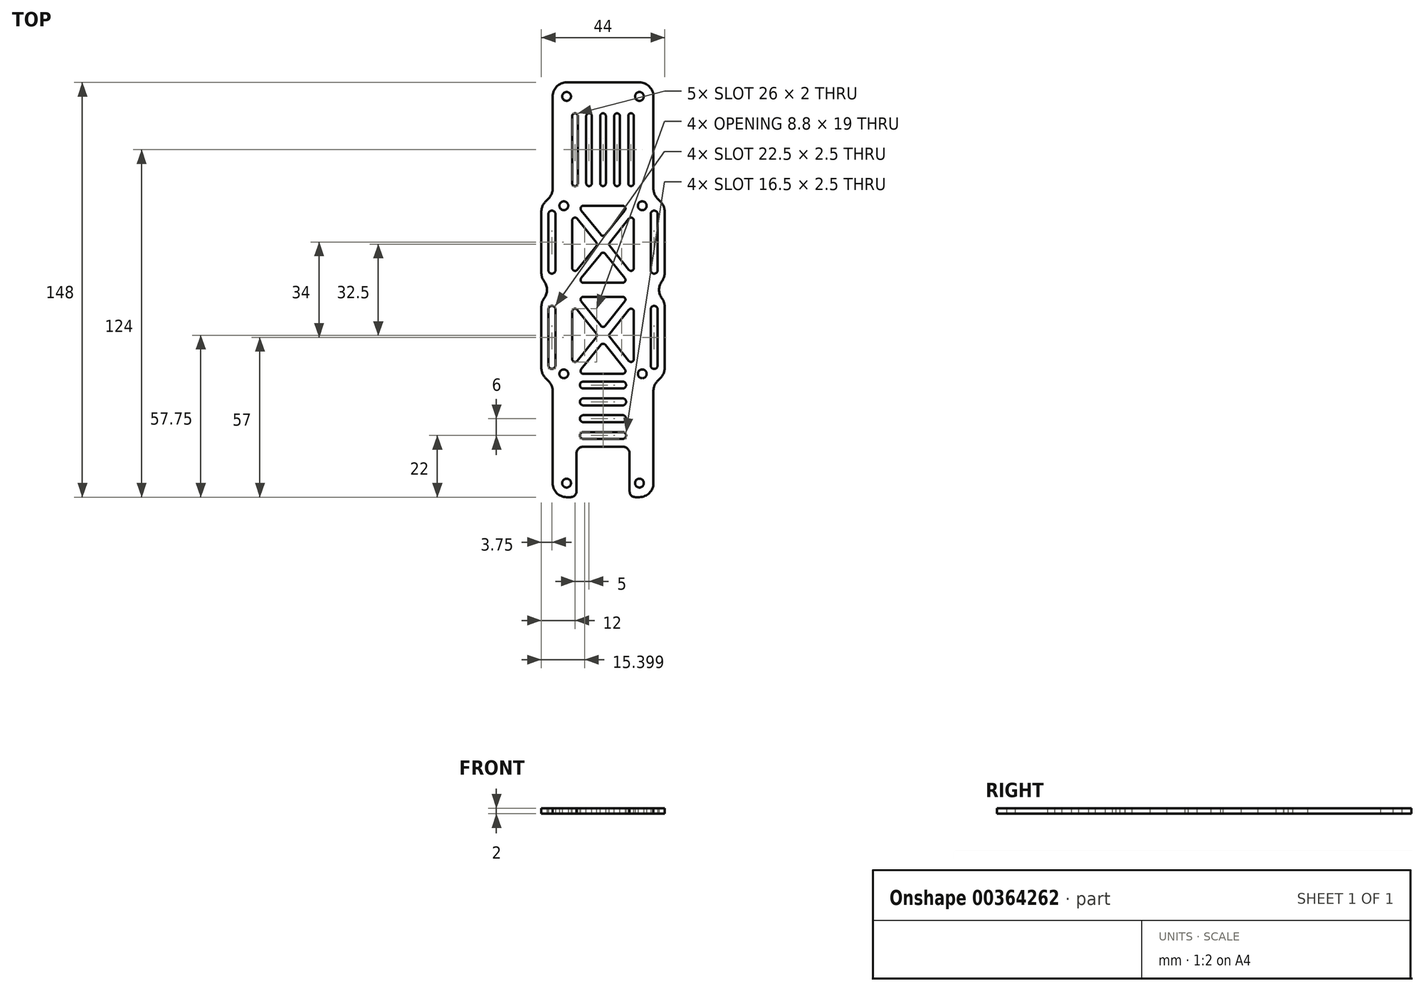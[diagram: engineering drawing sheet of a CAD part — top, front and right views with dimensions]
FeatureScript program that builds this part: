
annotation { "Feature Type Name" : "Feature", "Feature Type Description" : "" }
export const myFeature = defineFeature(function(context is Context, id is Id, definition is map)
    precondition{}
    {
        {
            var Q0;
            Q0=qCreatedBy(makeId("Top.planeOp"),FACE);
            var sketch = newSketch(context, id + "F0", { "sketchPlane" : qUnion([Q0])});
            skLineSegment(sketch, "E0", {"start": v(0, 74) * mm, "end": v(-13, 74) * mm});
            skLineSegment(sketch, "E1", {"start": v(-18, 69) * mm, "end": v(-18, 36.07) * mm});
            skLineSegment(sketch, "E2", {"start": v(-84.26, 70.7) * mm, "end": v(0, 0) * mm, "construction": true});
            skCircle(sketch, "E3", {"center": v(0, 0) * mm, "radius": 110 * mm, "construction": true});
            skPoint(sketch, "E4.visualSharp", {"position": v(-18, 74) * mm});
            skArc(sketch, "E4.filletArc", {"start": v(-13, 74) * mm, "mid": v(-16.54, 72.54) * mm, "end": v(-18, 69) * mm});
            skCircle(sketch, "E5", {"center": v(-13, 69) * mm, "radius": 1.57 * mm});
            skCircle(sketch, "E6.MirrorC", {"center": v(13, 69) * mm, "radius": 1.57 * mm});
            skArc(sketch, "E7.MirrorCS", {"start": v(13, 74) * mm, "mid": v(16.54, 72.54) * mm, "end": v(18, 69) * mm});
            skLineSegment(sketch, "E8.MirrorCS", {"start": v(0, 74) * mm, "end": v(13, 74) * mm});
            skLineSegment(sketch, "E9.MirrorCS", {"start": v(18, 69) * mm, "end": v(18, 36.07) * mm});
            skPoint(sketch, "E10.MirrorP", {"position": v(18, 74) * mm});
            skLineSegment(sketch, "E11.MirrorCS", {"start": v(84.26, 70.7) * mm, "end": v(0, 0) * mm, "construction": true});
            skArc(sketch, "E12.MirrorCS", {"start": v(-13, -74) * mm, "mid": v(-16.54, -72.54) * mm, "end": v(-18, -69) * mm});
            skLineSegment(sketch, "E13.MirrorCS", {"start": v(-11.5, -74) * mm, "end": v(-13, -74) * mm});
            skArc(sketch, "E14.MirrorCS", {"start": v(13, -74) * mm, "mid": v(16.54, -72.54) * mm, "end": v(18, -69) * mm});
            skLineSegment(sketch, "E15.MirrorCS", {"start": v(11.5, -74) * mm, "end": v(13, -74) * mm});
            skPoint(sketch, "E16.MirrorP", {"position": v(18, -74) * mm});
            skPoint(sketch, "E17.MirrorP", {"position": v(-18, -74) * mm});
            skLineSegment(sketch, "E18.MirrorCS", {"start": v(-18, -69) * mm, "end": v(-18, -36.07) * mm});
            skLineSegment(sketch, "E19.MirrorCS", {"start": v(18, -69) * mm, "end": v(18, -36.07) * mm});
            skCircle(sketch, "E20", {"center": v(-84.26, 70.7) * mm, "radius": 64.5 * mm, "construction": true});
            skCircle(sketch, "E21", {"center": v(-14, 30) * mm, "radius": 1.57 * mm});
            skCircle(sketch, "E22.MirrorC", {"center": v(14, 30) * mm, "radius": 1.57 * mm});
            skCircle(sketch, "E23.MirrorC", {"center": v(14, -30) * mm, "radius": 1.57 * mm});
            skCircle(sketch, "E24.MirrorC", {"center": v(-14, -30) * mm, "radius": 1.57 * mm});
            skLineSegment(sketch, "E25", {"start": v(-9.5, -72) * mm, "end": v(-9.5, -58.5) * mm});
            skLineSegment(sketch, "E26", {"start": v(-7, -56) * mm, "end": v(0, -56) * mm});
            skPoint(sketch, "E27.visualSharp", {"position": v(-9.5, -56) * mm});
            skArc(sketch, "E27.filletArc", {"start": v(-7, -56) * mm, "mid": v(-8.77, -56.73) * mm, "end": v(-9.5, -58.5) * mm});
            skLineSegment(sketch, "E28.MirrorCS", {"start": v(7, -56) * mm, "end": v(0, -56) * mm});
            skArc(sketch, "E29.MirrorCS", {"start": v(7, -56) * mm, "mid": v(8.77, -56.73) * mm, "end": v(9.5, -58.5) * mm});
            skLineSegment(sketch, "E30.MirrorCS", {"start": v(9.5, -72) * mm, "end": v(9.5, -58.5) * mm});
            skPoint(sketch, "E31.orphan", {"position": v(0, -74) * mm});
            skLineSegment(sketch, "E32", {"start": v(-22, 27.93) * mm, "end": v(-22, 6) * mm});
            skLineSegment(sketch, "E33", {"start": v(-20.54, 31.46) * mm, "end": v(-19.46, 32.54) * mm});
            skPoint(sketch, "E34.trimOffspring.end.orphan", {"position": v(-18, 0) * mm});
            skLineSegment(sketch, "E35.MirrorCS", {"start": v(-20.54, -31.46) * mm, "end": v(-19.46, -32.54) * mm});
            skLineSegment(sketch, "E36.MirrorCS", {"start": v(20.54, 31.46) * mm, "end": v(19.46, 32.54) * mm});
            skLineSegment(sketch, "E37.MirrorCS", {"start": v(22, 27.93) * mm, "end": v(22, 6) * mm});
            skLineSegment(sketch, "E38.MirrorCS", {"start": v(20.54, -31.46) * mm, "end": v(19.46, -32.54) * mm});
            skPoint(sketch, "E39.trimOffspring.end.orphan", {"position": v(18, 0) * mm});
            skPoint(sketch, "E40.visualSharp", {"position": v(-18, 34) * mm});
            skArc(sketch, "E40.filletArc", {"start": v(-19.46, 32.54) * mm, "mid": v(-18.38, 34.16) * mm, "end": v(-18, 36.07) * mm});
            skPoint(sketch, "E41.visualSharp", {"position": v(18, 34) * mm});
            skArc(sketch, "E41.filletArc", {"start": v(18, 36.07) * mm, "mid": v(18.38, 34.16) * mm, "end": v(19.46, 32.54) * mm});
            skPoint(sketch, "E42.visualSharp", {"position": v(22, 30) * mm});
            skArc(sketch, "E42.filletArc", {"start": v(22, 27.93) * mm, "mid": v(21.62, 29.84) * mm, "end": v(20.54, 31.46) * mm});
            skPoint(sketch, "E43.visualSharp", {"position": v(22, -30) * mm});
            skArc(sketch, "E43.filletArc", {"start": v(20.54, -31.46) * mm, "mid": v(21.62, -29.84) * mm, "end": v(22, -27.93) * mm});
            skPoint(sketch, "E44.visualSharp", {"position": v(18, -34) * mm});
            skArc(sketch, "E44.filletArc", {"start": v(19.46, -32.54) * mm, "mid": v(18.38, -34.16) * mm, "end": v(18, -36.07) * mm});
            skPoint(sketch, "E45.visualSharp", {"position": v(-18, -34) * mm});
            skArc(sketch, "E45.filletArc", {"start": v(-18, -36.07) * mm, "mid": v(-18.38, -34.16) * mm, "end": v(-19.46, -32.54) * mm});
            skPoint(sketch, "E46.visualSharp", {"position": v(-22, -30) * mm});
            skArc(sketch, "E46.filletArc", {"start": v(-22, -27.93) * mm, "mid": v(-21.62, -29.84) * mm, "end": v(-20.54, -31.46) * mm});
            skPoint(sketch, "E47.visualSharp", {"position": v(-22, 30) * mm});
            skArc(sketch, "E47.filletArc", {"start": v(-20.54, 31.46) * mm, "mid": v(-21.62, 29.84) * mm, "end": v(-22, 27.93) * mm});
            skLineSegment(sketch, "E48", {"start": v(-18.25, 27) * mm, "end": v(-18.25, 7) * mm, "construction": true});
            skArc(sketch, "E49.0.startCap", {"start": v(-19.5, 27) * mm, "mid": v(-18.25, 28.25) * mm, "end": v(-17, 27) * mm});
            skArc(sketch, "E49.0.endCap", {"start": v(-17, 7) * mm, "mid": v(-18.25, 5.75) * mm, "end": v(-19.5, 7) * mm});
            skLineSegment(sketch, "E49.0.left", {"start": v(-17, 27) * mm, "end": v(-17, 7) * mm});
            skLineSegment(sketch, "E49.0.right", {"start": v(-19.5, 27) * mm, "end": v(-19.5, 7) * mm});
            skLineSegment(sketch, "E50.MirrorCS", {"start": v(17, 27) * mm, "end": v(17, 7) * mm});
            skLineSegment(sketch, "E51.MirrorCS", {"start": v(19.5, 27) * mm, "end": v(19.5, 7) * mm});
            skArc(sketch, "E52.MirrorCS", {"start": v(17, 7) * mm, "mid": v(18.25, 5.75) * mm, "end": v(19.5, 7) * mm});
            skArc(sketch, "E53.MirrorCS", {"start": v(19.5, 27) * mm, "mid": v(18.25, 28.25) * mm, "end": v(17, 27) * mm});
            skLineSegment(sketch, "E54.MirrorCS", {"start": v(18.25, 27) * mm, "end": v(18.25, 7) * mm, "construction": true});
            skLineSegment(sketch, "E55.MirrorCS", {"start": v(19.5, -27) * mm, "end": v(19.5, -7) * mm});
            skArc(sketch, "E56.MirrorCS", {"start": v(17, -7) * mm, "mid": v(18.25, -5.75) * mm, "end": v(19.5, -7) * mm});
            skLineSegment(sketch, "E57.MirrorCS", {"start": v(17, -27) * mm, "end": v(17, -7) * mm});
            skLineSegment(sketch, "E58.MirrorCS", {"start": v(18.25, -27) * mm, "end": v(18.25, -7) * mm, "construction": true});
            skArc(sketch, "E59.MirrorCS", {"start": v(19.5, -27) * mm, "mid": v(18.25, -28.25) * mm, "end": v(17, -27) * mm});
            skLineSegment(sketch, "E60.MirrorCS", {"start": v(-17, -27) * mm, "end": v(-17, -7) * mm});
            skLineSegment(sketch, "E61.MirrorCS", {"start": v(-18.25, -27) * mm, "end": v(-18.25, -7) * mm, "construction": true});
            skArc(sketch, "E62.MirrorCS", {"start": v(-19.5, -27) * mm, "mid": v(-18.25, -28.25) * mm, "end": v(-17, -27) * mm});
            skLineSegment(sketch, "E63.MirrorCS", {"start": v(-19.5, -27) * mm, "end": v(-19.5, -7) * mm});
            skArc(sketch, "E64.MirrorCS", {"start": v(-17, -7) * mm, "mid": v(-18.25, -5.75) * mm, "end": v(-19.5, -7) * mm});
            skCircle(sketch, "E65", {"center": v(-13, -69) * mm, "radius": 1.57 * mm});
            skCircle(sketch, "E66.MirrorC", {"center": v(13, -69) * mm, "radius": 1.57 * mm});
            skArc(sketch, "E67", {"start": v(21, 3) * mm, "mid": v(20, 0) * mm, "end": v(21, -3) * mm});
            skLineSegment(sketch, "E68.trimOffspring", {"start": v(22, -6) * mm, "end": v(22, -27.93) * mm});
            skPoint(sketch, "E69.visualSharp", {"position": v(22, 4) * mm});
            skArc(sketch, "E69.filletArc", {"start": v(21, 3) * mm, "mid": v(21.74, 4.42) * mm, "end": v(22, 6) * mm});
            skPoint(sketch, "E70.visualSharp", {"position": v(22, -4) * mm});
            skArc(sketch, "E70.filletArc", {"start": v(22, -6) * mm, "mid": v(21.74, -4.42) * mm, "end": v(21, -3) * mm});
            skArc(sketch, "E71.MirrorCS", {"start": v(-21, 3) * mm, "mid": v(-20, 0) * mm, "end": v(-21, -3) * mm});
            skArc(sketch, "E72.MirrorCS", {"start": v(-21, 3) * mm, "mid": v(-21.74, 4.42) * mm, "end": v(-22, 6) * mm});
            skArc(sketch, "E73.MirrorCS", {"start": v(-22, -6) * mm, "mid": v(-21.74, -4.42) * mm, "end": v(-21, -3) * mm});
            skLineSegment(sketch, "E74.trimOffspring", {"start": v(-22, -6) * mm, "end": v(-22, -27.93) * mm});
            skPoint(sketch, "E75.visualSharp", {"position": v(-9.5, -74) * mm});
            skArc(sketch, "E75.filletArc", {"start": v(-11.5, -74) * mm, "mid": v(-10.09, -73.41) * mm, "end": v(-9.5, -72) * mm});
            skPoint(sketch, "E76.visualSharp", {"position": v(9.5, -74) * mm});
            skArc(sketch, "E76.filletArc", {"start": v(9.5, -72) * mm, "mid": v(10.09, -73.41) * mm, "end": v(11.5, -74) * mm});
            skSolve(sketch);
        }
        {
            var Q0;
            Q0=qSketchRegion(id+"F0",true);
            extrude(context, id + "F1", {"entities" : qUnion([Q0]), "depth" : 2 * mm, "offsetDistance" : 25 * mm});
        }
        {
            var Q0;
            Q0=makeQuery(id+"F1.opExtrude","CAP_FACE",FACE,{"disambiguationData":[OSD([sQuery(id+"F0.wireOp",EDGE,"E0"),sQuery(id+"F0.wireOp",EDGE,"E1"),sQuery(id+"F0.wireOp",EDGE,"E4.filletArc"),sQuery(id+"F0.wireOp",EDGE,"E5"),sQuery(id+"F0.wireOp",EDGE,"E6.MirrorC"),sQuery(id+"F0.wireOp",EDGE,"E7.MirrorCS"),sQuery(id+"F0.wireOp",EDGE,"E8.MirrorCS"),sQuery(id+"F0.wireOp",EDGE,"E9.MirrorCS"),sQuery(id+"F0.wireOp",EDGE,"E12.MirrorCS"),sQuery(id+"F0.wireOp",EDGE,"E13.MirrorCS"),sQuery(id+"F0.wireOp",EDGE,"E14.MirrorCS"),sQuery(id+"F0.wireOp",EDGE,"E15.MirrorCS"),sQuery(id+"F0.wireOp",EDGE,"E18.MirrorCS"),sQuery(id+"F0.wireOp",EDGE,"E19.MirrorCS"),sQuery(id+"F0.wireOp",EDGE,"E21"),sQuery(id+"F0.wireOp",EDGE,"E22.MirrorC"),sQuery(id+"F0.wireOp",EDGE,"E23.MirrorC"),sQuery(id+"F0.wireOp",EDGE,"E24.MirrorC"),sQuery(id+"F0.wireOp",EDGE,"E25"),sQuery(id+"F0.wireOp",EDGE,"E26"),sQuery(id+"F0.wireOp",EDGE,"E27.filletArc"),sQuery(id+"F0.wireOp",EDGE,"E28.MirrorCS"),sQuery(id+"F0.wireOp",EDGE,"E29.MirrorCS"),sQuery(id+"F0.wireOp",EDGE,"E30.MirrorCS"),sQuery(id+"F0.wireOp",EDGE,"E32"),sQuery(id+"F0.wireOp",EDGE,"E33"),sQuery(id+"F0.wireOp",EDGE,"E35.MirrorCS"),sQuery(id+"F0.wireOp",EDGE,"E36.MirrorCS"),sQuery(id+"F0.wireOp",EDGE,"E37.MirrorCS"),sQuery(id+"F0.wireOp",EDGE,"E38.MirrorCS"),sQuery(id+"F0.wireOp",EDGE,"E40.filletArc"),sQuery(id+"F0.wireOp",EDGE,"E41.filletArc"),sQuery(id+"F0.wireOp",EDGE,"E42.filletArc"),sQuery(id+"F0.wireOp",EDGE,"E43.filletArc"),sQuery(id+"F0.wireOp",EDGE,"E44.filletArc"),sQuery(id+"F0.wireOp",EDGE,"E45.filletArc"),sQuery(id+"F0.wireOp",EDGE,"E46.filletArc"),sQuery(id+"F0.wireOp",EDGE,"E47.filletArc"),sQuery(id+"F0.wireOp",EDGE,"E49.0.startCap"),sQuery(id+"F0.wireOp",EDGE,"E49.0.endCap"),sQuery(id+"F0.wireOp",EDGE,"E49.0.left"),sQuery(id+"F0.wireOp",EDGE,"E49.0.right"),sQuery(id+"F0.wireOp",EDGE,"E50.MirrorCS"),sQuery(id+"F0.wireOp",EDGE,"E51.MirrorCS"),sQuery(id+"F0.wireOp",EDGE,"E52.MirrorCS"),sQuery(id+"F0.wireOp",EDGE,"E53.MirrorCS"),sQuery(id+"F0.wireOp",EDGE,"E55.MirrorCS"),sQuery(id+"F0.wireOp",EDGE,"E56.MirrorCS"),sQuery(id+"F0.wireOp",EDGE,"E57.MirrorCS"),sQuery(id+"F0.wireOp",EDGE,"E59.MirrorCS"),sQuery(id+"F0.wireOp",EDGE,"E60.MirrorCS"),sQuery(id+"F0.wireOp",EDGE,"E62.MirrorCS"),sQuery(id+"F0.wireOp",EDGE,"E63.MirrorCS"),sQuery(id+"F0.wireOp",EDGE,"E64.MirrorCS"),sQuery(id+"F0.wireOp",EDGE,"6103eb4e-61a2-4ce9-9e73-76816fc0ace0.0.startCap"),sQuery(id+"F0.wireOp",EDGE,"6103eb4e-61a2-4ce9-9e73-76816fc0ace0.0.endCap"),sQuery(id+"F0.wireOp",EDGE,"6103eb4e-61a2-4ce9-9e73-76816fc0ace0.0.left"),sQuery(id+"F0.wireOp",EDGE,"6103eb4e-61a2-4ce9-9e73-76816fc0ace0.0.right"),sQuery(id+"F0.wireOp",EDGE,"954c3681-dcb8-4ed5-8d4a-031128a9d742.0.startCap"),sQuery(id+"F0.wireOp",EDGE,"954c3681-dcb8-4ed5-8d4a-031128a9d742.0.endCap"),sQuery(id+"F0.wireOp",EDGE,"954c3681-dcb8-4ed5-8d4a-031128a9d742.0.left"),sQuery(id+"F0.wireOp",EDGE,"954c3681-dcb8-4ed5-8d4a-031128a9d742.0.right"),sQuery(id+"F0.wireOp",EDGE,"f21f7b6c-da99-4986-b79a-1df9cf54cdf10.MirrorCS"),sQuery(id+"F0.wireOp",EDGE,"f21f7b6c-da99-4986-b79a-1df9cf54cdf11.MirrorCS"),sQuery(id+"F0.wireOp",EDGE,"f21f7b6c-da99-4986-b79a-1df9cf54cdf12.MirrorCS"),sQuery(id+"F0.wireOp",EDGE,"f21f7b6c-da99-4986-b79a-1df9cf54cdf13.MirrorCS"),sQuery(id+"F0.wireOp",EDGE,"f21f7b6c-da99-4986-b79a-1df9cf54cdf17.MirrorCS"),sQuery(id+"F0.wireOp",EDGE,"f21f7b6c-da99-4986-b79a-1df9cf54cdf18.MirrorCS"),sQuery(id+"F0.wireOp",EDGE,"f21f7b6c-da99-4986-b79a-1df9cf54cdf19.MirrorCS"),sQuery(id+"F0.wireOp",EDGE,"f21f7b6c-da99-4986-b79a-1df9cf54cdf110.MirrorCS"),sQuery(id+"F0.wireOp",EDGE,"E65"),sQuery(id+"F0.wireOp",EDGE,"E66.MirrorC"),sQuery(id+"F0.wireOp",EDGE,"E67"),sQuery(id+"F0.wireOp",EDGE,"E68.trimOffspring"),sQuery(id+"F0.wireOp",EDGE,"E69.filletArc"),sQuery(id+"F0.wireOp",EDGE,"E70.filletArc"),sQuery(id+"F0.wireOp",EDGE,"E71.MirrorCS"),sQuery(id+"F0.wireOp",EDGE,"E72.MirrorCS"),sQuery(id+"F0.wireOp",EDGE,"E73.MirrorCS"),sQuery(id+"F0.wireOp",EDGE,"E74.trimOffspring"),sQuery(id+"F0.wireOp",EDGE,"E75.filletArc"),sQuery(id+"F0.wireOp",EDGE,"E76.filletArc")])],"isStart":false});
            var sketch = newSketch(context, id + "F2", { "sketchPlane" : qUnion([Q0])});
            skLineSegment(sketch, "E77.bottom", {"start": v(-7, 30) * mm, "end": v(7, 30) * mm});
            skLineSegment(sketch, "E77.top", {"start": v(-7, 2.5) * mm, "end": v(7, 2.5) * mm});
            skLineSegment(sketch, "E77.left", {"start": v(-11, 24.75) * mm, "end": v(-11, 7.75) * mm});
            skLineSegment(sketch, "E77.right", {"start": v(11, 24.75) * mm, "end": v(11, 7.75) * mm});
            skLineSegment(sketch, "E78", {"start": v(11, 30) * mm, "end": v(-11, 2.5) * mm, "construction": true});
            skLineSegment(sketch, "E79", {"start": v(-11, 30) * mm, "end": v(11, 2.5) * mm, "construction": true});
            skLineSegment(sketch, "E80", {"start": v(-7.78, 28.38) * mm, "end": v(-0.78, 19.63) * mm});
            skLineSegment(sketch, "E81", {"start": v(-9.22, 25.37) * mm, "end": v(-2.42, 16.87) * mm});
            skLineSegment(sketch, "E82.MirrorCS", {"start": v(7.78, 28.38) * mm, "end": v(0.78, 19.63) * mm});
            skLineSegment(sketch, "E83.MirrorCS", {"start": v(9.22, 25.37) * mm, "end": v(2.42, 16.87) * mm});
            skLineSegment(sketch, "E84.trimOffspring", {"start": v(-2.42, 15.63) * mm, "end": v(-9.22, 7.13) * mm});
            skLineSegment(sketch, "E85.trimOffspring", {"start": v(0.78, 12.87) * mm, "end": v(7.78, 4.12) * mm});
            skLineSegment(sketch, "E86.trimOffspring", {"start": v(-0.78, 12.87) * mm, "end": v(-7.78, 4.12) * mm});
            skLineSegment(sketch, "E87.trimOffspring", {"start": v(2.42, 15.63) * mm, "end": v(9.22, 7.13) * mm});
            skPoint(sketch, "E88.visualSharp", {"position": v(-9.08, 30) * mm});
            skArc(sketch, "E88.filletArc", {"start": v(-7, 30) * mm, "mid": v(-7.9, 29.43) * mm, "end": v(-7.78, 28.38) * mm});
            skPoint(sketch, "E89.visualSharp", {"position": v(-11, 27.6) * mm});
            skArc(sketch, "E89.filletArc", {"start": v(-9.22, 25.37) * mm, "mid": v(-10.33, 25.7) * mm, "end": v(-11, 24.75) * mm});
            skPoint(sketch, "E90.visualSharp", {"position": v(9.08, 30) * mm});
            skArc(sketch, "E90.filletArc", {"start": v(7.78, 28.38) * mm, "mid": v(7.9, 29.43) * mm, "end": v(7, 30) * mm});
            skPoint(sketch, "E91.visualSharp", {"position": v(0, 18.65) * mm});
            skArc(sketch, "E91.filletArc", {"start": v(-0.78, 19.63) * mm, "mid": v(0, 19.25) * mm, "end": v(0.78, 19.63) * mm});
            skPoint(sketch, "E92.visualSharp", {"position": v(11, 27.6) * mm});
            skArc(sketch, "E92.filletArc", {"start": v(11, 24.75) * mm, "mid": v(10.33, 25.7) * mm, "end": v(9.22, 25.37) * mm});
            skPoint(sketch, "E93.visualSharp", {"position": v(1.92, 16.25) * mm});
            skArc(sketch, "E93.filletArc", {"start": v(2.42, 16.87) * mm, "mid": v(2.2, 16.25) * mm, "end": v(2.42, 15.63) * mm});
            skPoint(sketch, "E94.visualSharp", {"position": v(11, 4.9) * mm});
            skArc(sketch, "E94.filletArc", {"start": v(9.22, 7.13) * mm, "mid": v(10.33, 6.8) * mm, "end": v(11, 7.75) * mm});
            skPoint(sketch, "E95.visualSharp", {"position": v(9.08, 2.5) * mm});
            skArc(sketch, "E95.filletArc", {"start": v(7, 2.5) * mm, "mid": v(7.9, 3.07) * mm, "end": v(7.78, 4.12) * mm});
            skPoint(sketch, "E96.visualSharp", {"position": v(0, 13.85) * mm});
            skArc(sketch, "E96.filletArc", {"start": v(0.78, 12.87) * mm, "mid": v(0, 13.25) * mm, "end": v(-0.78, 12.87) * mm});
            skPoint(sketch, "E97.visualSharp", {"position": v(-9.08, 2.5) * mm});
            skArc(sketch, "E97.filletArc", {"start": v(-7.78, 4.12) * mm, "mid": v(-7.9, 3.07) * mm, "end": v(-7, 2.5) * mm});
            skPoint(sketch, "E98.visualSharp", {"position": v(-11, 4.9) * mm});
            skArc(sketch, "E98.filletArc", {"start": v(-11, 7.75) * mm, "mid": v(-10.33, 6.8) * mm, "end": v(-9.22, 7.13) * mm});
            skPoint(sketch, "E99.visualSharp", {"position": v(-1.92, 16.25) * mm});
            skArc(sketch, "E99.filletArc", {"start": v(-2.42, 15.63) * mm, "mid": v(-2.2, 16.25) * mm, "end": v(-2.42, 16.87) * mm});
            skArc(sketch, "E100.MirrorCS", {"start": v(-7.78, -4.12) * mm, "mid": v(-7.9, -3.07) * mm, "end": v(-7, -2.5) * mm});
            skArc(sketch, "E101.MirrorCS", {"start": v(0.78, -12.87) * mm, "mid": v(0, -13.25) * mm, "end": v(-0.78, -12.87) * mm});
            skArc(sketch, "E102.MirrorCS", {"start": v(11, -24.75) * mm, "mid": v(10.33, -25.7) * mm, "end": v(9.22, -25.37) * mm});
            skArc(sketch, "E103.MirrorCS", {"start": v(2.42, -16.87) * mm, "mid": v(2.2, -16.25) * mm, "end": v(2.42, -15.63) * mm});
            skArc(sketch, "E104.MirrorCS", {"start": v(9.22, -7.13) * mm, "mid": v(10.33, -6.8) * mm, "end": v(11, -7.75) * mm});
            skArc(sketch, "E105.MirrorCS", {"start": v(-2.42, -15.63) * mm, "mid": v(-2.2, -16.25) * mm, "end": v(-2.42, -16.87) * mm});
            skArc(sketch, "E106.MirrorCS", {"start": v(7, -2.5) * mm, "mid": v(7.9, -3.07) * mm, "end": v(7.78, -4.12) * mm});
            skArc(sketch, "E107.MirrorCS", {"start": v(-0.78, -19.63) * mm, "mid": v(0, -19.25) * mm, "end": v(0.78, -19.63) * mm});
            skArc(sketch, "E108.MirrorCS", {"start": v(-9.22, -25.37) * mm, "mid": v(-10.33, -25.7) * mm, "end": v(-11, -24.75) * mm});
            skArc(sketch, "E109.MirrorCS", {"start": v(7.78, -28.38) * mm, "mid": v(7.9, -29.43) * mm, "end": v(7, -30) * mm});
            skArc(sketch, "E110.MirrorCS", {"start": v(-7, -30) * mm, "mid": v(-7.9, -29.43) * mm, "end": v(-7.78, -28.38) * mm});
            skArc(sketch, "E111.MirrorCS", {"start": v(-11, -7.75) * mm, "mid": v(-10.33, -6.8) * mm, "end": v(-9.22, -7.13) * mm});
            skLineSegment(sketch, "E112.MirrorCS", {"start": v(-7, -2.5) * mm, "end": v(7, -2.5) * mm});
            skLineSegment(sketch, "E113.MirrorCS", {"start": v(-7, -30) * mm, "end": v(7, -30) * mm});
            skLineSegment(sketch, "E114.MirrorCS", {"start": v(11, -30) * mm, "end": v(-11, -2.5) * mm, "construction": true});
            skPoint(sketch, "E115.MirrorP", {"position": v(0, -13.85) * mm});
            skPoint(sketch, "E116.MirrorP", {"position": v(1.92, -16.25) * mm});
            skPoint(sketch, "E117.MirrorP", {"position": v(-1.92, -16.25) * mm});
            skPoint(sketch, "E118.MirrorP", {"position": v(-11, -4.9) * mm});
            skPoint(sketch, "E119.MirrorP", {"position": v(9.08, -30) * mm});
            skPoint(sketch, "E120.MirrorP", {"position": v(11, -27.6) * mm});
            skLineSegment(sketch, "E121.MirrorCS", {"start": v(-9.22, -25.37) * mm, "end": v(-2.42, -16.87) * mm});
            skLineSegment(sketch, "E122.MirrorCS", {"start": v(0.78, -12.87) * mm, "end": v(7.78, -4.12) * mm});
            skLineSegment(sketch, "E123.MirrorCS", {"start": v(-11, -30) * mm, "end": v(11, -2.5) * mm, "construction": true});
            skPoint(sketch, "E124.MirrorP", {"position": v(-9.08, -30) * mm});
            skPoint(sketch, "E125.MirrorP", {"position": v(-11, -27.6) * mm});
            skPoint(sketch, "E126.MirrorP", {"position": v(11, -4.9) * mm});
            skLineSegment(sketch, "E127.MirrorCS", {"start": v(-0.78, -12.87) * mm, "end": v(-7.78, -4.12) * mm});
            skPoint(sketch, "E128.MirrorP", {"position": v(0, -18.65) * mm});
            skLineSegment(sketch, "E129.MirrorCS", {"start": v(7.78, -28.38) * mm, "end": v(0.78, -19.63) * mm});
            skPoint(sketch, "E130.MirrorP", {"position": v(9.08, -2.5) * mm});
            skLineSegment(sketch, "E131.MirrorCS", {"start": v(9.22, -25.37) * mm, "end": v(2.42, -16.87) * mm});
            skLineSegment(sketch, "E132.MirrorCS", {"start": v(-2.42, -15.63) * mm, "end": v(-9.22, -7.13) * mm});
            skLineSegment(sketch, "E133.MirrorCS", {"start": v(11, -24.75) * mm, "end": v(11, -7.75) * mm});
            skLineSegment(sketch, "E134.MirrorCS", {"start": v(-11, -24.75) * mm, "end": v(-11, -7.75) * mm});
            skPoint(sketch, "E135.MirrorP", {"position": v(-9.08, -2.5) * mm});
            skLineSegment(sketch, "E136.MirrorCS", {"start": v(-7.78, -28.38) * mm, "end": v(-0.78, -19.63) * mm});
            skLineSegment(sketch, "E137.MirrorCS", {"start": v(2.42, -15.63) * mm, "end": v(9.22, -7.13) * mm});
            skLineSegment(sketch, "E138", {"start": v(-18, 50) * mm, "end": v(18, 50) * mm, "construction": true});
            skLineSegment(sketch, "E139", {"start": v(-10, 62) * mm, "end": v(-10, 38) * mm, "construction": true});
            skLineSegment(sketch, "E140.1.0.0", {"start": v(-5, 62) * mm, "end": v(-5, 38) * mm, "construction": true});
            skLineSegment(sketch, "E140.2.0.0", {"start": v(0, 62) * mm, "end": v(0, 38) * mm, "construction": true});
            skLineSegment(sketch, "E140.3.0.0", {"start": v(5, 62) * mm, "end": v(5, 38) * mm, "construction": true});
            skLineSegment(sketch, "E140.4.0.0", {"start": v(10, 62) * mm, "end": v(10, 38) * mm, "construction": true});
            skLineSegment(sketch, "E140.direction1", {"start": v(-10, 38) * mm, "end": v(-5, 38) * mm, "construction": true});
            skArc(sketch, "E141.0.startCap", {"start": v(-11, 62) * mm, "mid": v(-10, 63) * mm, "end": v(-9, 62) * mm});
            skArc(sketch, "E141.0.endCap", {"start": v(-9, 38) * mm, "mid": v(-10, 37) * mm, "end": v(-11, 38) * mm});
            skLineSegment(sketch, "E141.0.left", {"start": v(-9, 62) * mm, "end": v(-9, 38) * mm});
            skLineSegment(sketch, "E141.0.right", {"start": v(-11, 62) * mm, "end": v(-11, 38) * mm});
            skArc(sketch, "E141.1.startCap", {"start": v(-6, 62) * mm, "mid": v(-5, 63) * mm, "end": v(-4, 62) * mm});
            skArc(sketch, "E141.1.endCap", {"start": v(-4, 38) * mm, "mid": v(-5, 37) * mm, "end": v(-6, 38) * mm});
            skLineSegment(sketch, "E141.1.left", {"start": v(-4, 62) * mm, "end": v(-4, 38) * mm});
            skLineSegment(sketch, "E141.1.right", {"start": v(-6, 62) * mm, "end": v(-6, 38) * mm});
            skArc(sketch, "E141.2.startCap", {"start": v(-1, 62) * mm, "mid": v(0, 63) * mm, "end": v(1, 62) * mm});
            skArc(sketch, "E141.2.endCap", {"start": v(1, 38) * mm, "mid": v(0, 37) * mm, "end": v(-1, 38) * mm});
            skLineSegment(sketch, "E141.2.left", {"start": v(1, 62) * mm, "end": v(1, 38) * mm});
            skLineSegment(sketch, "E141.2.right", {"start": v(-1, 62) * mm, "end": v(-1, 38) * mm});
            skArc(sketch, "E141.3.startCap", {"start": v(4, 62) * mm, "mid": v(5, 63) * mm, "end": v(6, 62) * mm});
            skArc(sketch, "E141.3.endCap", {"start": v(6, 38) * mm, "mid": v(5, 37) * mm, "end": v(4, 38) * mm});
            skLineSegment(sketch, "E141.3.left", {"start": v(6, 62) * mm, "end": v(6, 38) * mm});
            skLineSegment(sketch, "E141.3.right", {"start": v(4, 62) * mm, "end": v(4, 38) * mm});
            skArc(sketch, "E141.4.startCap", {"start": v(9, 62) * mm, "mid": v(10, 63) * mm, "end": v(11, 62) * mm});
            skArc(sketch, "E141.4.endCap", {"start": v(11, 38) * mm, "mid": v(10, 37) * mm, "end": v(9, 38) * mm});
            skLineSegment(sketch, "E141.4.left", {"start": v(11, 62) * mm, "end": v(11, 38) * mm});
            skLineSegment(sketch, "E141.4.right", {"start": v(9, 62) * mm, "end": v(9, 38) * mm});
            skLineSegment(sketch, "E142", {"start": v(-7, -52) * mm, "end": v(7, -52) * mm, "construction": true});
            skLineSegment(sketch, "E143.0.1.0", {"start": v(-7, -46) * mm, "end": v(7, -46) * mm, "construction": true});
            skLineSegment(sketch, "E143.0.2.0", {"start": v(-7, -40) * mm, "end": v(7, -40) * mm, "construction": true});
            skLineSegment(sketch, "E143.0.3.0", {"start": v(-7, -34) * mm, "end": v(7, -34) * mm, "construction": true});
            skLineSegment(sketch, "E143.direction1", {"start": v(-7, -52) * mm, "end": v(13, -52) * mm, "construction": true});
            skLineSegment(sketch, "E143.direction2", {"start": v(-7, -52) * mm, "end": v(-7, -46) * mm, "construction": true});
            skArc(sketch, "E144.0.startCap", {"start": v(-7, -53.25) * mm, "mid": v(-8.25, -52) * mm, "end": v(-7, -50.75) * mm});
            skArc(sketch, "E144.0.endCap", {"start": v(7, -50.75) * mm, "mid": v(8.25, -52) * mm, "end": v(7, -53.25) * mm});
            skLineSegment(sketch, "E144.0.left", {"start": v(-7, -50.75) * mm, "end": v(7, -50.75) * mm});
            skLineSegment(sketch, "E144.0.right", {"start": v(-7, -53.25) * mm, "end": v(7, -53.25) * mm});
            skArc(sketch, "E145.0.startCap", {"start": v(-7, -47.25) * mm, "mid": v(-8.25, -46) * mm, "end": v(-7, -44.75) * mm});
            skArc(sketch, "E145.0.endCap", {"start": v(7, -44.75) * mm, "mid": v(8.25, -46) * mm, "end": v(7, -47.25) * mm});
            skLineSegment(sketch, "E145.0.left", {"start": v(-7, -44.75) * mm, "end": v(7, -44.75) * mm});
            skLineSegment(sketch, "E145.0.right", {"start": v(-7, -47.25) * mm, "end": v(7, -47.25) * mm});
            skArc(sketch, "E145.1.startCap", {"start": v(-7, -41.25) * mm, "mid": v(-8.25, -40) * mm, "end": v(-7, -38.75) * mm});
            skArc(sketch, "E145.1.endCap", {"start": v(7, -38.75) * mm, "mid": v(8.25, -40) * mm, "end": v(7, -41.25) * mm});
            skLineSegment(sketch, "E145.1.left", {"start": v(-7, -38.75) * mm, "end": v(7, -38.75) * mm});
            skLineSegment(sketch, "E145.1.right", {"start": v(-7, -41.25) * mm, "end": v(7, -41.25) * mm});
            skArc(sketch, "E145.2.startCap", {"start": v(-7, -35.25) * mm, "mid": v(-8.25, -34) * mm, "end": v(-7, -32.75) * mm});
            skArc(sketch, "E145.2.endCap", {"start": v(7, -32.75) * mm, "mid": v(8.25, -34) * mm, "end": v(7, -35.25) * mm});
            skLineSegment(sketch, "E145.2.left", {"start": v(-7, -32.75) * mm, "end": v(7, -32.75) * mm});
            skLineSegment(sketch, "E145.2.right", {"start": v(-7, -35.25) * mm, "end": v(7, -35.25) * mm});
            skSolve(sketch);
        }
        {
            var Q0;
            Q0 = qSketchRegion(id + "F2", true);
            extrude(context, id + "F3", {"entities" : qUnion([Q0]), "operationType" : NewBodyOperationType.REMOVE, "oppositeDirection" : true, "depth" : 25 * mm, "offsetDistance" : 25 * mm});
        }
    });
